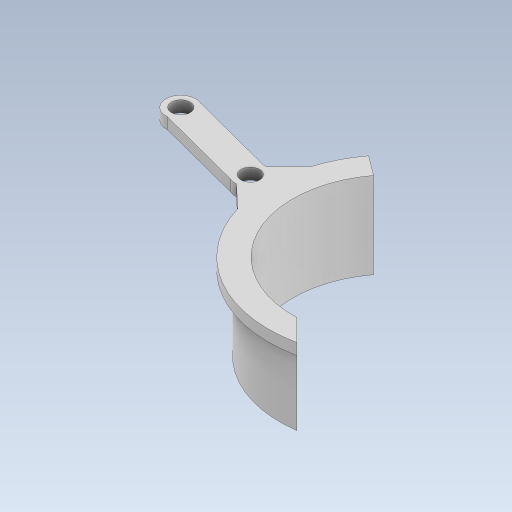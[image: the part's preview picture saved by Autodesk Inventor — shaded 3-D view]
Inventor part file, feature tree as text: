
AUTODESK INVENTOR PART (.ipt)
format: ipt  version: 2023.5 (Build 275446000, 446)  size: 325,120 bytes
history: native  units: mm
features: extrude x2, sketch x1
ambient origin geometry x8: Origin, YZ Plane, XZ Plane, XY Plane, X Axis, Y Axis, Z Axis, Center Point
bodies: Body1 (feature_tree)
feature tree (3):
  sketch  "Sketch1"  dims[d41=3.0mm d42=0.0mm d43=3.0mm d44=20.0mm d45=0.0mm d46=0.0mm d47=5.0mm d48=33.5mm d49=30.5mm d50=29.0mm d51=66.999922mm d52=5.883847mm d53=5.883847mm d54=25.572922mm d55=25.572922mm d56=8.0mm d57=5.0mm d58=8.0mm d59=54.0mm d60=20.0mm d61=45.0deg]
  extrude  "Extrusion5"  Depth=3.0mm TaperAngle=0.0deg
  extrude  "Extrusion6"  Depth=20.0mm
